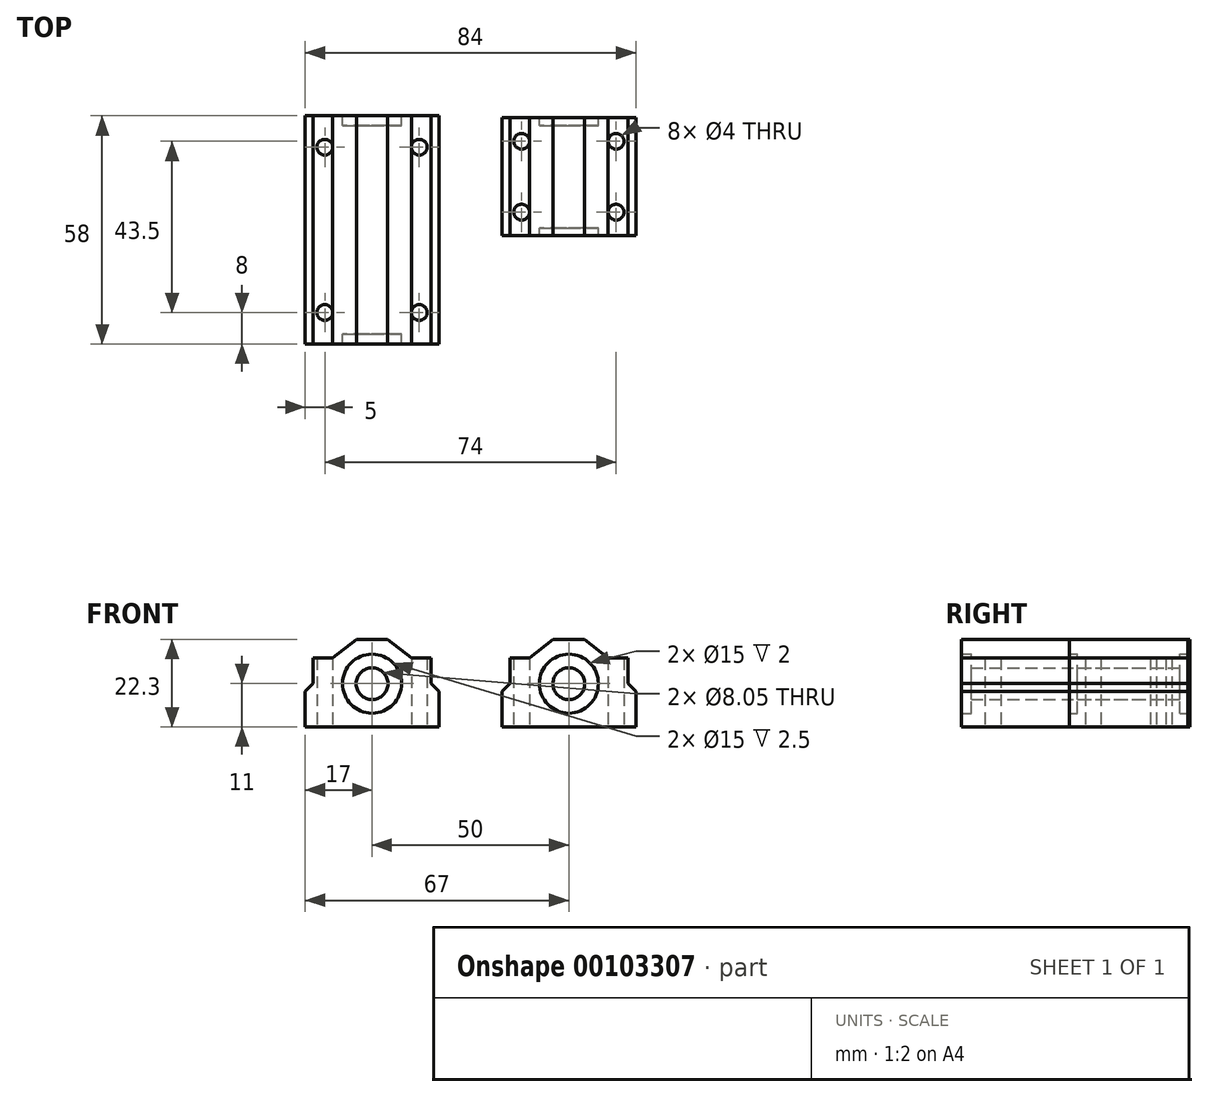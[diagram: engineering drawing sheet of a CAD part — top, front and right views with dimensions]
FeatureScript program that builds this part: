
annotation { "Feature Type Name" : "Feature", "Feature Type Description" : "" }
export const myFeature = defineFeature(function(context is Context, id is Id, definition is map)
    precondition{}
    {
        {
            var Q0;
            Q0=qCreatedBy(makeId("Front.planeOp"),FACE);
            var sketch = newSketch(context, id + "F0", { "sketchPlane" : qUnion([Q0])});
            skLineSegment(sketch, "E0.top", {"start": v(-17, 0) * mm, "end": v(17, 0) * mm});
            skLineSegment(sketch, "E0.left", {"start": v(-17, 9) * mm, "end": v(-17, 0) * mm});
            skLineSegment(sketch, "E0.right", {"start": v(17, 9) * mm, "end": v(17, 0) * mm});
            skLineSegment(sketch, "E1.bottom", {"start": v(-15, 17.5) * mm, "end": v(-10, 17.5) * mm});
            skLineSegment(sketch, "E1.left", {"start": v(-15, 17.5) * mm, "end": v(-15, 11) * mm});
            skLineSegment(sketch, "E1.right", {"start": v(15, 17.5) * mm, "end": v(15, 11) * mm});
            skLineSegment(sketch, "E2.bottom", {"start": v(-4, 22.3) * mm, "end": v(4, 22.3) * mm});
            skLineSegment(sketch, "E3.trimOffspring", {"start": v(10, 17.5) * mm, "end": v(15, 17.5) * mm});
            skLineSegment(sketch, "E4", {"start": v(0, 28.44) * mm, "end": v(0, -9.73) * mm, "construction": true});
            skLineSegment(sketch, "E5", {"start": v(-27.68, 11) * mm, "end": v(22.32, 11) * mm, "construction": true});
            skPoint(sketch, "E6", {"position": v(0, 11) * mm});
            skCircle(sketch, "E7", {"center": v(0, 11) * mm, "radius": 4.03 * mm});
            skCircle(sketch, "E8", {"center": v(0, 11) * mm, "radius": 7.5 * mm});
            skLineSegment(sketch, "E9", {"start": v(-4, 22.3) * mm, "end": v(-10, 17.5) * mm});
            skLineSegment(sketch, "E10", {"start": v(4, 22.3) * mm, "end": v(10, 17.5) * mm});
            skLineSegment(sketch, "E11", {"start": v(-17, 9) * mm, "end": v(-15, 11) * mm});
            skLineSegment(sketch, "E12", {"start": v(17, 9) * mm, "end": v(15, 11) * mm});
            skLineSegment(sketch, "E13.top", {"start": v(33, 0) * mm, "end": v(67, 0) * mm});
            skLineSegment(sketch, "E13.left", {"start": v(33, 9) * mm, "end": v(33, 0) * mm});
            skLineSegment(sketch, "E13.right", {"start": v(67, 9) * mm, "end": v(67, 0) * mm});
            skLineSegment(sketch, "E14.bottom", {"start": v(35, 17.5) * mm, "end": v(40, 17.5) * mm});
            skLineSegment(sketch, "E14.left", {"start": v(35, 17.5) * mm, "end": v(35, 11) * mm});
            skLineSegment(sketch, "E14.right", {"start": v(65, 17.5) * mm, "end": v(65, 11) * mm});
            skLineSegment(sketch, "E15.bottom", {"start": v(46, 22.3) * mm, "end": v(54, 22.3) * mm});
            skLineSegment(sketch, "E16.trimOffspring", {"start": v(60, 17.5) * mm, "end": v(65, 17.5) * mm});
            skLineSegment(sketch, "E17", {"start": v(50, 28.64) * mm, "end": v(50, -9.53) * mm, "construction": true});
            skLineSegment(sketch, "E18", {"start": v(22.32, 11) * mm, "end": v(74.93, 11) * mm, "construction": true});
            skPoint(sketch, "E19", {"position": v(50, 11) * mm});
            skCircle(sketch, "E20", {"center": v(50, 11) * mm, "radius": 4.03 * mm});
            skCircle(sketch, "E21", {"center": v(50, 11) * mm, "radius": 7.5 * mm});
            skLineSegment(sketch, "E22", {"start": v(46, 22.3) * mm, "end": v(40, 17.5) * mm});
            skLineSegment(sketch, "E23", {"start": v(54, 22.3) * mm, "end": v(60, 17.5) * mm});
            skLineSegment(sketch, "E24", {"start": v(33, 9) * mm, "end": v(35, 11) * mm});
            skLineSegment(sketch, "E25", {"start": v(67, 9) * mm, "end": v(65, 11) * mm});
            skSolve(sketch);
        }
        {
            var Q0;
            Q0=makeQuery(id+"F0.imprint","IMPRINT",FACE,{"disambiguationData":[TD([[makeQuery(id+"F0.imprint","IMPRINT",EDGE,{"derivedFrom":sQuery(id+"F0.wireOp",EDGE,"E0.top")}),1.0]])]});
            extrude(context, id + "F1", {"entities" : qUnion([Q0]), "depth" : 55.5 * mm, "hasSecondDirection" : true, "secondDirectionOppositeDirection" : true, "secondDirectionDepth" : 2.5 * mm});
        }
        {
            var Q0;
            Q0=makeQuery(id+"F0.imprint","IMPRINT",FACE,{"disambiguationData":[TD([[makeQuery(id+"F0.imprint","IMPRINT",EDGE,{"derivedFrom":sQuery(id+"F0.wireOp",EDGE,"E7")}),-1.0]])]});
            extrude(context, id + "F2", {"entities" : qUnion([Q0]), "operationType" : NewBodyOperationType.ADD, "depth" : 53 * mm});
        }
        {
            var Q0;
            Q0=makeQuery(id+"F0.imprint","IMPRINT",FACE,{"disambiguationData":[TD([[makeQuery(id+"F0.imprint","IMPRINT",EDGE,{"derivedFrom":sQuery(id+"F0.wireOp",EDGE,"E13.top")}),1.0]])]});
            extrude(context, id + "F3", {"entities" : qUnion([Q0]), "depth" : 28 * mm, "hasSecondDirection" : true, "secondDirectionOppositeDirection" : true, "secondDirectionDepth" : 2 * mm});
        }
        {
            var Q0;
            Q0=makeQuery(id+"F0.imprint","IMPRINT",FACE,{"disambiguationData":[TD([[makeQuery(id+"F0.imprint","IMPRINT",EDGE,{"derivedFrom":sQuery(id+"F0.wireOp",EDGE,"E20")}),-1.0]])]});
            extrude(context, id + "F4", {"entities" : qUnion([Q0]), "operationType" : NewBodyOperationType.ADD, "depth" : 26 * mm});
        }
        {
            var Q0;
            Q0=qCreatedBy(makeId("Top.planeOp"),FACE);
            var sketch = newSketch(context, id + "F5", { "sketchPlane" : qUnion([Q0])});
            skLineSegment(sketch, "E26", {"start": v(-12, -56.9) * mm, "end": v(-12, 17.56) * mm, "construction": true});
            skLineSegment(sketch, "E27", {"start": v(12, -57.11) * mm, "end": v(12, 17.97) * mm, "construction": true});
            skLineSegment(sketch, "E28", {"start": v(-24.87, -47.5) * mm, "end": v(24.77, -47.5) * mm, "construction": true});
            skLineSegment(sketch, "E29", {"start": v(-23.84, -5.5) * mm, "end": v(24.39, -5.5) * mm, "construction": true});
            skLineSegment(sketch, "E30", {"start": v(-25.04, -26.5) * mm, "end": v(26.16, -26.5) * mm, "construction": true});
            skCircle(sketch, "E31", {"center": v(-12, -47.5) * mm, "radius": 2 * mm});
            skCircle(sketch, "E32", {"center": v(12, -47.5) * mm, "radius": 2 * mm});
            skCircle(sketch, "E33", {"center": v(-12, -5.5) * mm, "radius": 2 * mm});
            skCircle(sketch, "E34", {"center": v(12, -5.5) * mm, "radius": 2 * mm});
            skLineSegment(sketch, "E35", {"start": v(38, -30.82) * mm, "end": v(38, 8.7) * mm, "construction": true});
            skLineSegment(sketch, "E36", {"start": v(62, -30.82) * mm, "end": v(62, 8.7) * mm, "construction": true});
            skLineSegment(sketch, "E37", {"start": v(50, -30.82) * mm, "end": v(50, 8.7) * mm, "construction": true});
            skLineSegment(sketch, "E38", {"start": v(30.08, -22) * mm, "end": v(69.84, -22) * mm, "construction": true});
            skLineSegment(sketch, "E39", {"start": v(30.08, -13) * mm, "end": v(69.84, -13) * mm, "construction": true});
            skLineSegment(sketch, "E40", {"start": v(30.08, -4) * mm, "end": v(69.84, -4) * mm, "construction": true});
            skCircle(sketch, "E41", {"center": v(38, -22) * mm, "radius": 2 * mm});
            skCircle(sketch, "E42", {"center": v(62, -22) * mm, "radius": 2 * mm});
            skCircle(sketch, "E43", {"center": v(62, -4) * mm, "radius": 2 * mm});
            skCircle(sketch, "E44", {"center": v(38, -4) * mm, "radius": 2 * mm});
            skSolve(sketch);
        }
        {
            var Q0;
            Q0=makeQuery(id+"F5.imprint","IMPRINT",FACE,{"disambiguationData":[TD([[makeQuery(id+"F5.imprint","IMPRINT",EDGE,{"derivedFrom":sQuery(id+"F5.wireOp",EDGE,"E32")}),1.0]])]});
            var Q1;
            Q1=makeQuery(id+"F5.imprint","IMPRINT",FACE,{"disambiguationData":[TD([[makeQuery(id+"F5.imprint","IMPRINT",EDGE,{"derivedFrom":sQuery(id+"F5.wireOp",EDGE,"E31")}),1.0]])]});
            var Q2;
            Q2=makeQuery(id+"F5.imprint","IMPRINT",FACE,{"disambiguationData":[TD([[makeQuery(id+"F5.imprint","IMPRINT",EDGE,{"derivedFrom":sQuery(id+"F5.wireOp",EDGE,"E33")}),1.0]])]});
            var Q3;
            Q3=makeQuery(id+"F5.imprint","IMPRINT",FACE,{"disambiguationData":[TD([[makeQuery(id+"F5.imprint","IMPRINT",EDGE,{"derivedFrom":sQuery(id+"F5.wireOp",EDGE,"E34")}),1.0]])]});
            var Q4;
            Q4=makeQuery(id+"F5.imprint","IMPRINT",FACE,{"disambiguationData":[TD([[makeQuery(id+"F5.imprint","IMPRINT",EDGE,{"derivedFrom":sQuery(id+"F5.wireOp",EDGE,"E41")}),1.0]])]});
            var Q5;
            Q5=makeQuery(id+"F5.imprint","IMPRINT",FACE,{"disambiguationData":[TD([[makeQuery(id+"F5.imprint","IMPRINT",EDGE,{"derivedFrom":sQuery(id+"F5.wireOp",EDGE,"E42")}),1.0]])]});
            var Q6;
            Q6=makeQuery(id+"F5.imprint","IMPRINT",FACE,{"disambiguationData":[TD([[makeQuery(id+"F5.imprint","IMPRINT",EDGE,{"derivedFrom":sQuery(id+"F5.wireOp",EDGE,"E43")}),1.0]])]});
            var Q7;
            Q7=makeQuery(id+"F5.imprint","IMPRINT",FACE,{"disambiguationData":[TD([[makeQuery(id+"F5.imprint","IMPRINT",EDGE,{"derivedFrom":sQuery(id+"F5.wireOp",EDGE,"E44")}),1.0]])]});
            extrude(context, id + "F6", {"entities" : qUnion([Q0, Q1, Q2, Q3, Q4, Q5, Q6, Q7]), "operationType" : NewBodyOperationType.REMOVE, "endBound" : BoundingType.THROUGH_ALL, "depth" : 25 * mm});
        }
        {
            var Q0;
            Q0=makeQuery(id+"F5.imprint","IMPRINT",FACE,{"disambiguationData":[TD([[makeQuery(id+"F5.imprint","IMPRINT",EDGE,{"derivedFrom":sQuery(id+"F5.wireOp",EDGE,"E41")}),1.0]])]});
            var Q1;
            Q1=makeQuery(id+"F5.imprint","IMPRINT",FACE,{"disambiguationData":[TD([[makeQuery(id+"F5.imprint","IMPRINT",EDGE,{"derivedFrom":sQuery(id+"F5.wireOp",EDGE,"E42")}),1.0]])]});
            var Q2;
            Q2=makeQuery(id+"F5.imprint","IMPRINT",FACE,{"disambiguationData":[TD([[makeQuery(id+"F5.imprint","IMPRINT",EDGE,{"derivedFrom":sQuery(id+"F5.wireOp",EDGE,"E43")}),1.0]])]});
            var Q3;
            Q3=makeQuery(id+"F5.imprint","IMPRINT",FACE,{"disambiguationData":[TD([[makeQuery(id+"F5.imprint","IMPRINT",EDGE,{"derivedFrom":sQuery(id+"F5.wireOp",EDGE,"E44")}),1.0]])]});
            extrude(context, id + "F7", {"entities" : qUnion([Q0, Q1, Q2, Q3]), "operationType" : NewBodyOperationType.REMOVE, "endBound" : BoundingType.THROUGH_ALL, "depth" : 25 * mm});
        }
    });
